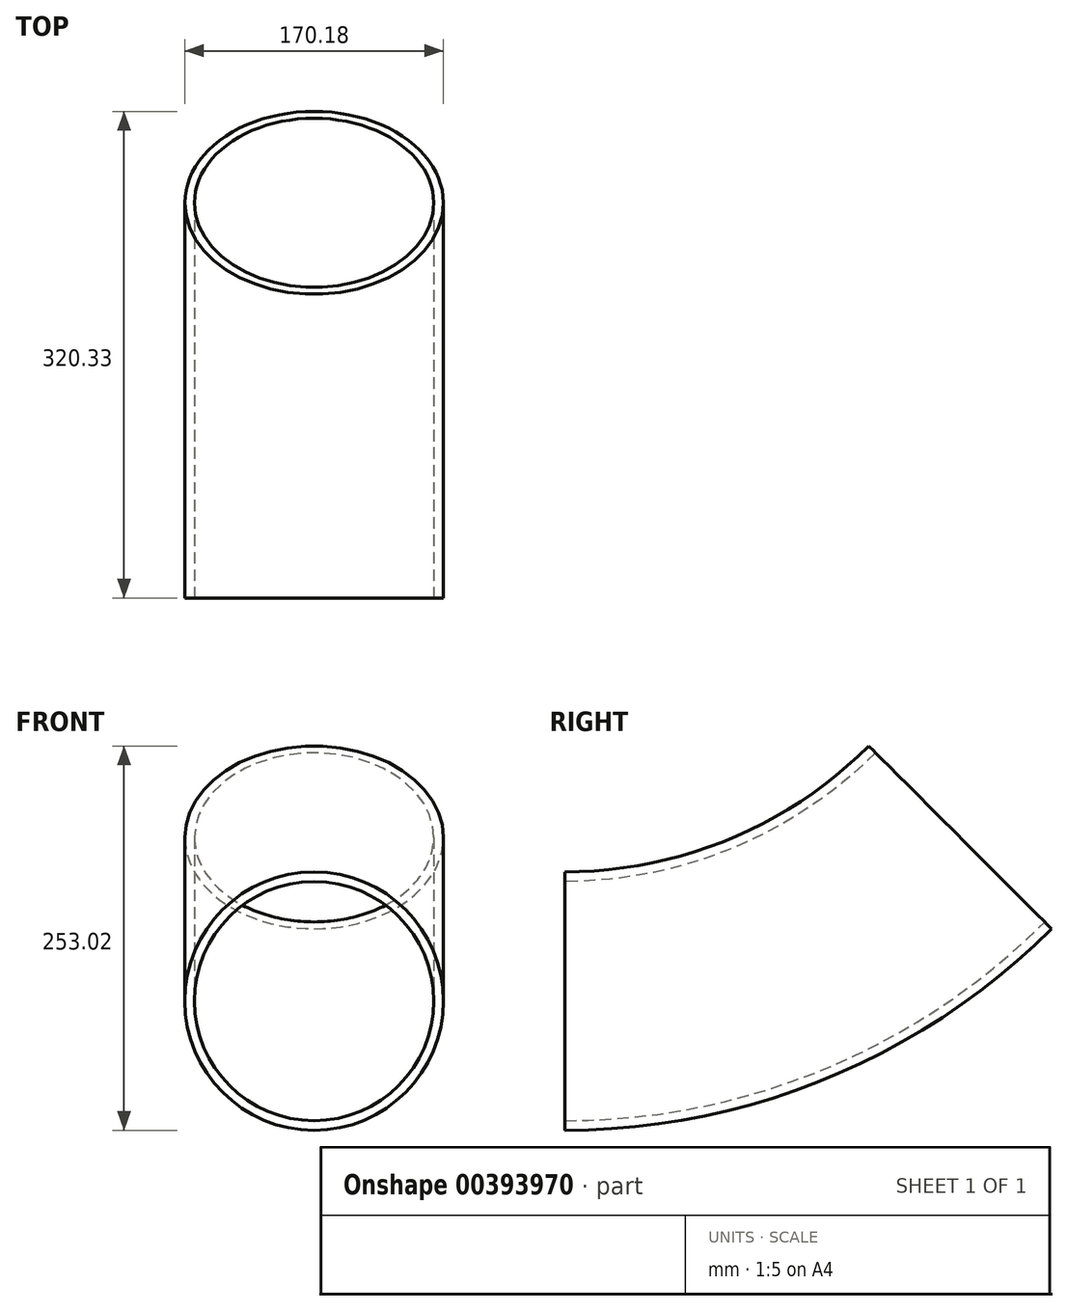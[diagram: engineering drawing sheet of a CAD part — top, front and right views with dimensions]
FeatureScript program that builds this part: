
annotation { "Feature Type Name" : "Feature", "Feature Type Description" : "" }
export const myFeature = defineFeature(function(context is Context, id is Id, definition is map)
    precondition{}
    {
        {
            var Q0;
            Q0=qCreatedBy(makeId("Front.planeOp"),FACE);
            var sketch = newSketch(context, id + "F0", { "sketchPlane" : qUnion([Q0])});
            skCircle(sketch, "E0", {"center": v(0, 0) * mm, "radius": 85.1 * mm});
            skCircle(sketch, "E1", {"center": v(0, 0) * mm, "radius": 78.74 * mm});
            skSolve(sketch);
        }
        {
            var Q0;
            Q0=qCreatedBy(makeId("Right.planeOp"),FACE);
            var sketch = newSketch(context, id + "F1", { "sketchPlane" : qUnion([Q0])});
            skLineSegment(sketch, "E2", {"start": v(0, 0) * mm, "end": v(152.4, 0) * mm, "construction": true});
            skLineSegment(sketch, "E3", {"start": v(152.4, 0) * mm, "end": v(260.16, 107.76) * mm, "construction": true});
            skArc(sketch, "E4", {"start": v(0, 0) * mm, "mid": v(140.8, 28) * mm, "end": v(260.16, 107.76) * mm});
            skSolve(sketch);
        }
        {
            var Q0;
            Q0 = qSketchRegion(id + "F0", true);
            var Q1;
            Q1 = qConstructionFilter(qBodyType(qCreatedBy(id + "F1" ,EDGE), BodyType.WIRE), ConstructionObject.NO);
            sweep(context, id + "F2", {"profiles" : qUnion([Q0]), "path" : qUnion([Q1])});
        }
    });
